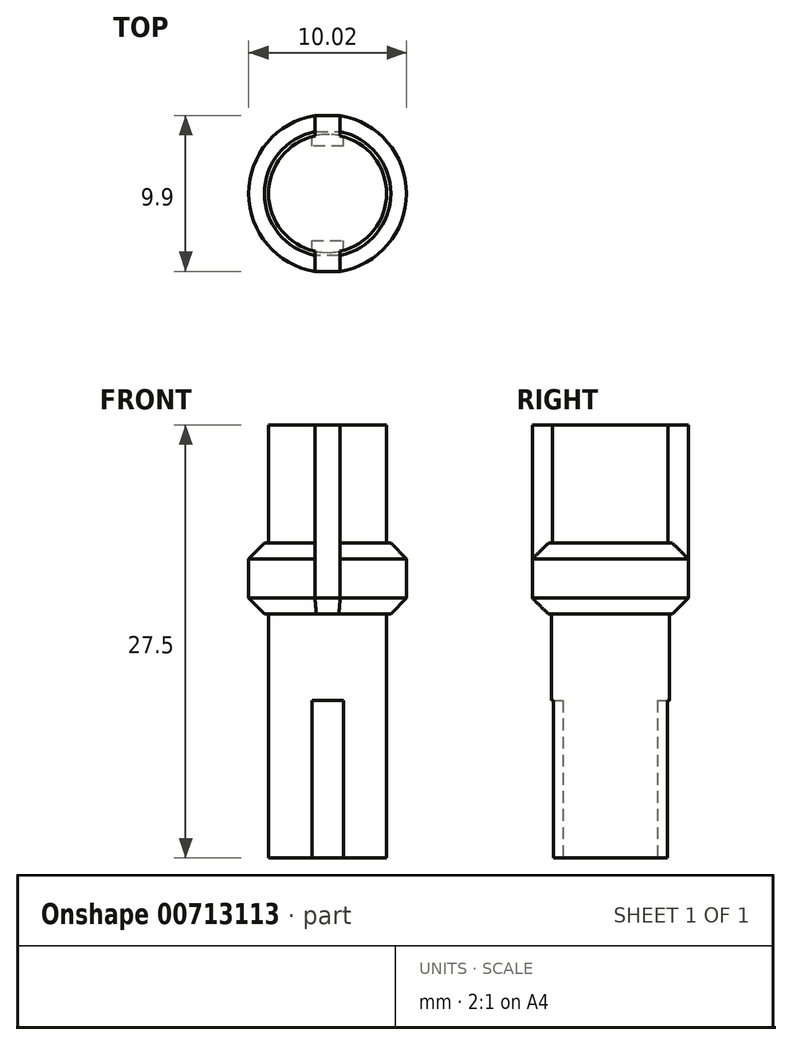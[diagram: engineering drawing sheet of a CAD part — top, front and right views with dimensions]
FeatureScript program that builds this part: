
annotation { "Feature Type Name" : "Feature", "Feature Type Description" : "" }
export const myFeature = defineFeature(function(context is Context, id is Id, definition is map)
    precondition{}
    {
        {
            var Q0;
            Q0=qCreatedBy(makeId("Top.planeOp"),FACE);
            var sketch = newSketch(context, id + "F0", { "sketchPlane" : qUnion([Q0])});
            skCircle(sketch, "E0", {"center": v(0, 0) * mm, "radius": 3.75 * mm});
            skLineSegment(sketch, "E1.bottom", {"start": v(0.8, 4.95) * mm, "end": v(-0.8, 4.95) * mm});
            skLineSegment(sketch, "E1.top", {"start": v(0.8, -4.95) * mm, "end": v(-0.8, -4.95) * mm});
            skLineSegment(sketch, "E1.left", {"start": v(0.8, 4.95) * mm, "end": v(0.8, -4.95) * mm});
            skLineSegment(sketch, "E1.right", {"start": v(-0.8, 4.95) * mm, "end": v(-0.8, -4.95) * mm});
            skCircle(sketch, "E2", {"center": v(0, 0) * mm, "radius": 5.01 * mm});
            skSolve(sketch);
        }
        {
            var Q0;
            {var subQ0=sQuery(id+"F0.wireOp",EDGE,"E1.left");var subQ1=sQuery(id+"F0.wireOp",EDGE,"E0");var subQ2=makeQuery(id+"F0.imprint","INTERSECT",VERTEX,{"disambiguationData":[OD(0.0)],"derivedFrom":[subQ1,subQ0]});Q0=makeQuery(id+"F0.imprint","IMPRINT",FACE,{"disambiguationData":[TD([[makeQuery(id+"F0.imprint","IMPRINT",EDGE,{"disambiguationData":[TD([[subQ2,1.0]])],"derivedFrom":subQ1}),1.0]])]});}
            var Q1;
            {var subQ0=sQuery(id+"F0.wireOp",EDGE,"E1.right");var subQ1=sQuery(id+"F0.wireOp",EDGE,"E0");var subQ2=makeQuery(id+"F0.imprint","INTERSECT",VERTEX,{"disambiguationData":[OD(0.0)],"derivedFrom":[subQ1,subQ0]});Q1=makeQuery(id+"F0.imprint","IMPRINT",FACE,{"disambiguationData":[TD([[makeQuery(id+"F0.imprint","IMPRINT",EDGE,{"disambiguationData":[TD([[subQ2,1.0]])],"derivedFrom":subQ1}),1.0]])]});}
            var Q2;
            {var subQ0=sQuery(id+"F0.wireOp",EDGE,"E1.right");var subQ1=sQuery(id+"F0.wireOp",EDGE,"E0");var subQ2=makeQuery(id+"F0.imprint","INTERSECT",VERTEX,{"disambiguationData":[OD(0.0)],"derivedFrom":[subQ1,subQ0]});Q2=makeQuery(id+"F0.imprint","IMPRINT",FACE,{"disambiguationData":[TD([[makeQuery(id+"F0.imprint","IMPRINT",EDGE,{"disambiguationData":[TD([[subQ2,-1.0]])],"derivedFrom":subQ1}),1.0]])]});}
            extrude(context, id + "F1", {"entities" : qUnion([Q0, Q1, Q2]), "oppositeDirection" : true, "depth" : 20 * mm, "offsetDistance" : 25 * mm});
        }
        {
            var Q0;
            {var subQ0=sQuery(id+"F0.wireOp",EDGE,"E1.left");var subQ1=sQuery(id+"F0.wireOp",EDGE,"E0");var subQ2=makeQuery(id+"F0.imprint","INTERSECT",VERTEX,{"disambiguationData":[OD(0.0)],"derivedFrom":[subQ1,subQ0]});Q0=makeQuery(id+"F0.imprint","IMPRINT",FACE,{"disambiguationData":[TD([[makeQuery(id+"F0.imprint","IMPRINT",EDGE,{"disambiguationData":[TD([[subQ2,1.0]])],"derivedFrom":subQ1}),1.0]])]});}
            var Q1;
            {var subQ0=sQuery(id+"F0.wireOp",EDGE,"E1.right");var subQ1=sQuery(id+"F0.wireOp",EDGE,"E0");var subQ2=makeQuery(id+"F0.imprint","INTERSECT",VERTEX,{"disambiguationData":[OD(0.0)],"derivedFrom":[subQ1,subQ0]});Q1=makeQuery(id+"F0.imprint","IMPRINT",FACE,{"disambiguationData":[TD([[makeQuery(id+"F0.imprint","IMPRINT",EDGE,{"disambiguationData":[TD([[subQ2,1.0]])],"derivedFrom":subQ1}),1.0]])]});}
            var Q2;
            {var subQ0=sQuery(id+"F0.wireOp",EDGE,"E1.right");var subQ1=sQuery(id+"F0.wireOp",EDGE,"E0");var subQ2=makeQuery(id+"F0.imprint","INTERSECT",VERTEX,{"disambiguationData":[OD(0.0)],"derivedFrom":[subQ1,subQ0]});Q2=makeQuery(id+"F0.imprint","IMPRINT",FACE,{"disambiguationData":[TD([[makeQuery(id+"F0.imprint","IMPRINT",EDGE,{"disambiguationData":[TD([[subQ2,-1.0]])],"derivedFrom":subQ1}),1.0]])]});}
            var Q3;
            {var subQ5=sQuery(id+"F0.wireOp",EDGE,"E1.bottom");Q3=makeQuery(id+"F0.imprint","IMPRINT",FACE,{"disambiguationData":[TD([[makeQuery(id+"F0.imprint","IMPRINT",EDGE,{"derivedFrom":subQ5}),1.0]])]});}
            var Q4;
            {var subQ5=sQuery(id+"F0.wireOp",EDGE,"E1.top");Q4=makeQuery(id+"F0.imprint","IMPRINT",FACE,{"disambiguationData":[TD([[makeQuery(id+"F0.imprint","IMPRINT",EDGE,{"derivedFrom":subQ5}),-1.0]])]});}
            extrude(context, id + "F2", {"entities" : qUnion([Q0, Q1, Q2, Q3, Q4]), "operationType" : NewBodyOperationType.ADD, "depth" : 7.5 * mm, "offsetDistance" : 25 * mm});
        }
        {
            var Q0;
            {var subQ0=sQuery(id+"F0.wireOp",EDGE,"E1.left");var subQ1=sQuery(id+"F0.wireOp",EDGE,"E0");var subQ2=makeQuery(id+"F0.imprint","INTERSECT",VERTEX,{"disambiguationData":[OD(0.0)],"derivedFrom":[subQ1,subQ0]});Q0=makeQuery(id+"F0.imprint","IMPRINT",FACE,{"disambiguationData":[TD([[makeQuery(id+"F0.imprint","IMPRINT",EDGE,{"disambiguationData":[TD([[subQ2,1.0]])],"derivedFrom":subQ1}),-1.0]])]});}
            var Q1;
            {var subQ5=sQuery(id+"F0.wireOp",EDGE,"E1.top");Q1=makeQuery(id+"F0.imprint","IMPRINT",FACE,{"disambiguationData":[TD([[makeQuery(id+"F0.imprint","IMPRINT",EDGE,{"derivedFrom":subQ5}),-1.0]])]});}
            var Q2;
            {var subQ0=sQuery(id+"F0.wireOp",EDGE,"E1.right");var subQ1=sQuery(id+"F0.wireOp",EDGE,"E0");var subQ2=makeQuery(id+"F0.imprint","INTERSECT",VERTEX,{"disambiguationData":[OD(0.0)],"derivedFrom":[subQ1,subQ0]});Q2=makeQuery(id+"F0.imprint","IMPRINT",FACE,{"disambiguationData":[TD([[makeQuery(id+"F0.imprint","IMPRINT",EDGE,{"disambiguationData":[TD([[subQ2,-1.0]])],"derivedFrom":subQ1}),-1.0]])]});}
            var Q3;
            {var subQ5=sQuery(id+"F0.wireOp",EDGE,"E1.bottom");Q3=makeQuery(id+"F0.imprint","IMPRINT",FACE,{"disambiguationData":[TD([[makeQuery(id+"F0.imprint","IMPRINT",EDGE,{"derivedFrom":subQ5}),1.0]])]});}
            extrude(context, id + "F3", {"entities" : qUnion([Q0, Q1, Q2, Q3]), "operationType" : NewBodyOperationType.ADD, "oppositeDirection" : true, "depth" : 4.5 * mm, "offsetDistance" : 25 * mm});
        }
        {
            var Q0;
            {var subQ0=sQuery(id+"F0.wireOp",EDGE,"E2");var subQ1=sQuery(id+"F0.wireOp",EDGE,"E1.right");Q0=makeQuery(id+"F3.opExtrude","CAP_EDGE",EDGE,{"disambiguationData":[OSD([subQ0]),TDD([makeQuery(id+"F0.imprint","IMPRINT",EDGE,{"disambiguationData":[TD([[makeQuery(id+"F0.imprint","INTERSECT",VERTEX,{"derivedFrom":[sQuery(id+"F0.wireOp",EDGE,"E1.bottom"),subQ1,subQ0]}),-1.0]])],"derivedFrom":subQ0})])],"isStart":false});}
            var Q1;
            {var subQ0=sQuery(id+"F0.wireOp",EDGE,"E2");var subQ1=sQuery(id+"F0.wireOp",EDGE,"E1.left");Q1=makeQuery(id+"F3.opExtrude","CAP_EDGE",EDGE,{"disambiguationData":[OSD([subQ0]),TDD([makeQuery(id+"F0.imprint","IMPRINT",EDGE,{"disambiguationData":[TD([[makeQuery(id+"F0.imprint","INTERSECT",VERTEX,{"derivedFrom":[sQuery(id+"F0.wireOp",EDGE,"E1.bottom"),subQ1,subQ0]}),1.0]])],"derivedFrom":subQ0})])],"isStart":false});}
            var Q2;
            Q2=makeQuery(id+"F3.opExtrude","CAP_EDGE",EDGE,{"disambiguationData":[OSD([sQuery(id+"F0.wireOp",EDGE,"E1.top")])],"isStart":false});
            var Q3;
            Q3=makeQuery(id+"F3.opExtrude","CAP_EDGE",EDGE,{"disambiguationData":[OSD([sQuery(id+"F0.wireOp",EDGE,"E1.bottom")])],"isStart":false});
            var Q4;
            {var subQ0=sQuery(id+"F0.wireOp",EDGE,"E2");var subQ1=sQuery(id+"F0.wireOp",EDGE,"E1.right");Q4=makeQuery(id+"F3.opExtrude","CAP_EDGE",EDGE,{"disambiguationData":[OSD([subQ0]),TDD([makeQuery(id+"F0.imprint","IMPRINT",EDGE,{"disambiguationData":[TD([[makeQuery(id+"F0.imprint","INTERSECT",VERTEX,{"derivedFrom":[sQuery(id+"F0.wireOp",EDGE,"E1.bottom"),subQ1,subQ0]}),-1.0]])],"derivedFrom":subQ0})])],"isStart":true});}
            var Q5;
            {var subQ0=sQuery(id+"F0.wireOp",EDGE,"E2");var subQ1=sQuery(id+"F0.wireOp",EDGE,"E1.left");Q5=makeQuery(id+"F3.opExtrude","CAP_EDGE",EDGE,{"disambiguationData":[OSD([subQ0]),TDD([makeQuery(id+"F0.imprint","IMPRINT",EDGE,{"disambiguationData":[TD([[makeQuery(id+"F0.imprint","INTERSECT",VERTEX,{"derivedFrom":[sQuery(id+"F0.wireOp",EDGE,"E1.bottom"),subQ1,subQ0]}),1.0]])],"derivedFrom":subQ0})])],"isStart":true});}
            chamfer(context, id + "F4", {"entities" : qUnion([Q0, Q1, Q2, Q3, Q4, Q5]), "width" : 1 * mm, "tangentPropagation" : true});
        }
        {
            var Q0;
            Q0=makeQuery(id+"F1.opExtrude","CAP_FACE",FACE,{"disambiguationData":[OSD([sQuery(id+"F0.wireOp",EDGE,"E0")])],"isStart":false});
            var sketch = newSketch(context, id + "F5", { "sketchPlane" : qUnion([Q0])});
            skLineSegment(sketch, "E3.bottom", {"start": v(1, 4) * mm, "end": v(-1, 4) * mm});
            skLineSegment(sketch, "E3.top", {"start": v(1, -4) * mm, "end": v(-1, -4) * mm});
            skLineSegment(sketch, "E3.left", {"start": v(1, 4) * mm, "end": v(1, -4) * mm});
            skLineSegment(sketch, "E3.right", {"start": v(-1, 4) * mm, "end": v(-1, -4) * mm});
            skPoint(sketch, "E3.middle", {"position": v(0, 0) * mm});
            skLineSegment(sketch, "E4.bottom", {"start": v(-1, 4) * mm, "end": v(1, 4) * mm});
            skLineSegment(sketch, "E4.top", {"start": v(-1, 3) * mm, "end": v(1, 3) * mm});
            skLineSegment(sketch, "E4.left", {"start": v(-1, 4) * mm, "end": v(-1, 3) * mm});
            skLineSegment(sketch, "E4.right", {"start": v(1, 4) * mm, "end": v(1, 3) * mm});
            skLineSegment(sketch, "E5.top", {"start": v(1, -3) * mm, "end": v(-1, -3) * mm});
            skLineSegment(sketch, "E5.left", {"start": v(1, -4) * mm, "end": v(1, -3) * mm});
            skLineSegment(sketch, "E5.right", {"start": v(-1, -4) * mm, "end": v(-1, -3) * mm});
            skSolve(sketch);
        }
        {
            var Q0;
            {var subQ0=sQuery(id+"F5.wireOp",EDGE,"E5.top");Q0=makeQuery(id+"F5.imprint","IMPRINT",FACE,{"disambiguationData":[TD([[makeQuery(id+"F5.imprint","IMPRINT",EDGE,{"derivedFrom":subQ0}),1.0]])]});}
            var Q1;
            {var subQ0=sQuery(id+"F5.wireOp",EDGE,"E4.top");Q1=makeQuery(id+"F5.imprint","IMPRINT",FACE,{"disambiguationData":[TD([[makeQuery(id+"F5.imprint","IMPRINT",EDGE,{"derivedFrom":subQ0}),1.0]])]});}
            extrude(context, id + "F6", {"entities" : qUnion([Q0, Q1]), "operationType" : NewBodyOperationType.REMOVE, "oppositeDirection" : true, "depth" : 10 * mm, "offsetDistance" : 25 * mm});
        }
    });
